# Revit family: Bathroom-Accessory-Waterworks-Flyte-Towel_Bar
name_source: partatom
category: Specialty Equipment
revit_build: Autodesk Revit MEP 2014 (Build: 20140709_2115(x64)
units: mm (PartAtom-declared; Revit-internal decimal feet)

## types (8) — shared parameters
Assembly Code = C1030200
Default Elevation = 3' - 0"
Depth = 0' - 3 7/16"
Height = 0' - 2 3/8"
Keynote = 22 40 00
Manufacturer = Waterworks
Product Documentation Link = http://assets.waterworks.com
Product Page URL = http://www.waterworks.com
URL = http://www.waterworks.com
Version = 2014 - v1.0a
Warranty = http://www.waterworks.com
‌Installation Requirements or Notes = Wall Mounted. Not designed to be field cut

## per-type parameters (varying)
| type | 18" Towel Bar | 24" Towel Bar | Constraint | ControlM | Finish | Length | Model | Model SKU | Product Name |
| Flyte 18” Single Towel Bar in Chrome | Yes | No | 1 | 1 | Metal - Waterworks - Chrome | 1' - 6" | FLTB18 | 22-43130-77563 | Flyte 18” Single Towel Bar |
| Flyte 18” Single Towel Bar in Graphite | Yes | No | 1 | 2 | Metal - Waterworks - Graphite | 1' - 6" | FLTB18 | 22-39098-92336 | Flyte 18” Single Towel Bar |
| Flyte 18” Single Towel Bar in Nickel | Yes | No | 1 | 3 | Metal - Waterworks - Nickel | 1' - 6" | FLTB18 | 22-39227-49736 | Flyte 18” Single Towel Bar |
| Flyte 18” Single Towel Bar in Unlacquered Brass | Yes | No | 1 | 4 | Metal - Waterworks - Unlacquered Brass | 1' - 6" | FLTB18 | 22-06174-67356 | Flyte 18” Single Towel Bar |
| Flyte 24” Single Towel Bar in Chrome | No | Yes | 2 | 5 | Metal - Waterworks - Chrome | 2' - 0" | FLTB24 | 22-50059-19662 | Flyte 24” Single Towel Bar |
| Flyte 24” Single Towel Bar in Graphite | No | Yes | 2 | 6 | Metal - Waterworks - Graphite | 2' - 0" | FLTB24 | 22-99807-78273 | Flyte 24” Single Towel Bar |
| Flyte 24” Single Towel Bar in Nickel | No | Yes | 2 | 7 | Metal - Waterworks - Nickel | 2' - 0" | FLTB24 | 22-50228-09742 | Flyte 24” Single Towel Bar |
| Flyte 24” Single Towel Bar in Unlacquered Brass | No | Yes | 2 | 8 | Metal - Waterworks - Unlacquered Brass | 2' - 0" | FLTB24 | 22-59402-53813 | Flyte 24” Single Towel Bar |

note: column(s) folded — value = type name in every type: Description

## geometry (parser evidence)
native form markers: Sweep x3
no freeform markers — native parametric forms only
